# Revit family: Toilet_Seat-Elongated_Closed_Front-KOHLER-Harken-K-22697T
name_source: partatom
category: Specialty Equipment
units: mm (PartAtom-declared; Revit-internal decimal feet)

## family parameters
Cut with Voids When Loaded = No
Host = Face
OmniClass Number = 23.31.19.19.17
OmniClass Title = Water Closet Seats
Part Type = Normal
Room Calculation Point = No
Round Connector Dimension = Use Diameter
Shared = No

## types (2) — shared parameters
ADA Compliant = No
Assembly Code = C1030200
Date Modified = 09/08/2022
Default Elevation = 15"
Description = Quiet-Close Seat (Truffle)
Height = 2 15/16"
Length = 18 3/16"
Manufacturer = Kohler Co.
Master Format 2014 = 10 28 00
Master Format 2014 Name = Toilet, Bath, and Laundry Accessories
Material = Plastic
Product Name = Harken
URL = http://www.kohler.com.cn
WaterSense Certified = No
Width = 14 7/16"

## per-type parameters (varying)
| type | Finish | Model | Type |
| 0-White | Kohler-Plastic-0-White | K-22697T-0 | 1 |
| TRF-Truffle | Kohler-Plastic-TRF-Truffle | K-22697T-TRF | 2 |

## geometry (parser evidence)
native form markers: Sweep x8
no freeform markers — native parametric forms only
